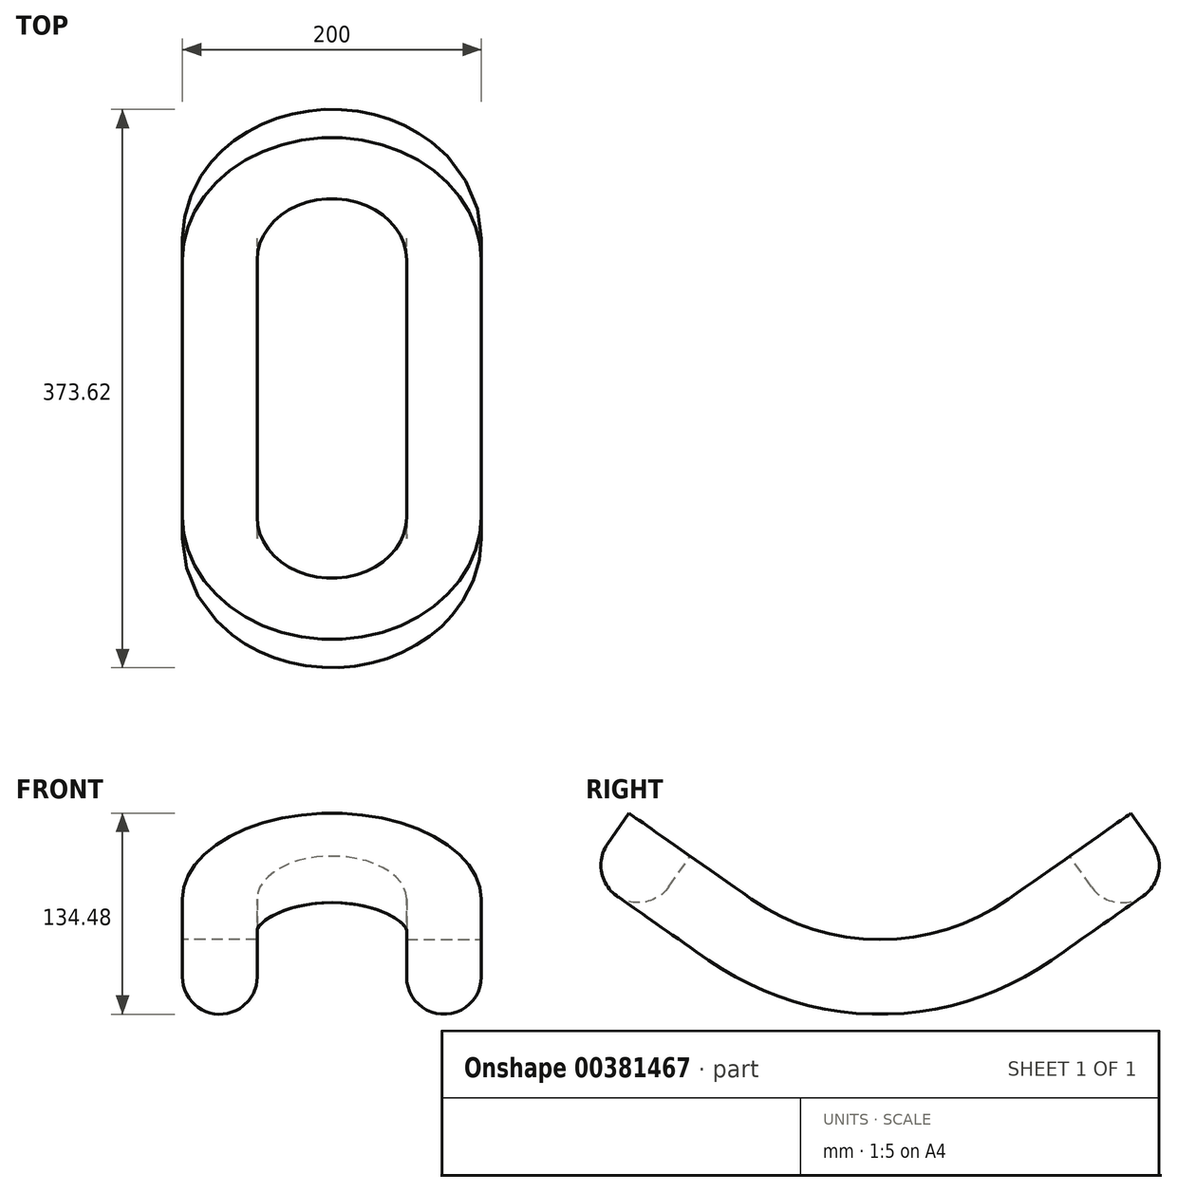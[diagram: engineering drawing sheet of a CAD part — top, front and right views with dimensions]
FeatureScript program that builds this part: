
annotation { "Feature Type Name" : "Feature", "Feature Type Description" : "" }
export const myFeature = defineFeature(function(context is Context, id is Id, definition is map)
    precondition{}
    {
        {
            var Q0;
            Q0=qCreatedBy(makeId("Right.planeOp"),FACE);
            var sketch = newSketch(context, id + "F0", { "sketchPlane" : qUnion([Q0])});
            skArc(sketch, "E0", {"start": v(0, 0) * mm, "mid": v(45.1, 6.94) * mm, "end": v(86.04, 27.13) * mm});
            skLineSegment(sketch, "E1", {"start": v(86.04, 27.13) * mm, "end": v(167.95, 84.48) * mm});
            skLineSegment(sketch, "E2", {"start": v(0, 0) * mm, "end": v(0, 150) * mm, "construction": true});
            skLineSegment(sketch, "E3", {"start": v(0, 150) * mm, "end": v(86.04, 27.13) * mm, "construction": true});
            skSolve(sketch);
        }
        {
            var Q0;
            Q0 = qConstructionFilter(qBodyType(qCreatedBy(id + "F0" ,EDGE), BodyType.WIRE), ConstructionObject.NO);
            extrude(context, id + "F1", {"bodyType" : ToolBodyType.SURFACE, "surfaceEntities" : qUnion([Q0]), "depth" : 100 * mm});
        }
        {
            var Q0;
            Q0=qCreatedBy(makeId("Front.planeOp"),FACE);
            var sketch = newSketch(context, id + "F2", { "sketchPlane" : qUnion([Q0])});
            skLineSegment(sketch, "E4.bottom", {"start": v(50, 0) * mm, "end": v(100, 0) * mm});
            skLineSegment(sketch, "E4.top", {"start": v(50, -25) * mm, "end": v(100, -25) * mm, "construction": true});
            skLineSegment(sketch, "E4.left", {"start": v(50, 0) * mm, "end": v(50, -25) * mm});
            skLineSegment(sketch, "E4.right", {"start": v(100, 0) * mm, "end": v(100, -25) * mm});
            skArc(sketch, "E5", {"start": v(50, -25) * mm, "mid": v(75, -50) * mm, "end": v(100, -25) * mm});
            skSolve(sketch);
        }
        {
            var Q0;
            Q0=makeQuery(id+"F1.opExtrude","SWEPT_FACE",FACE,{"disambiguationData":[OSD([sQuery(id+"F0.wireOp",EDGE,"E1")])]});
            var sketch = newSketch(context, id + "F3", { "sketchPlane" : qUnion([Q0])});
            skArc(sketch, "E6", {"start": v(100, -86.04) * mm, "mid": v(70.71, -156.75) * mm, "end": v(0, -186.04) * mm});
            skSolve(sketch);
        }
        {
            var Q0;
            Q0=makeQuery(id+"F2.imprint","IMPRINT",FACE,{"disambiguationData":[TD([[makeQuery(id+"F2.imprint","IMPRINT",EDGE,{"derivedFrom":sQuery(id+"F2.wireOp",EDGE,"E4.bottom")}),-1.0]])]});
            var Q1;
            Q1=makeQuery(id+"F1.opExtrude","CAP_EDGE",EDGE,{"disambiguationData":[OSD([sQuery(id+"F0.wireOp",EDGE,"E0")])],"isStart":false});
            var Q2;
            Q2=sQuery(id+"F3.wireOp",EDGE,"E6");
            sweep(context, id + "F4", {"profiles" : qUnion([Q0]), "path" : qUnion([Q1, Q2])});
        }
        {
            var Q0;
            Q0=makeQuery(id+"F4.opSweep","SWEPT_BODY",BODY,{"disambiguationData":[OSD([sQuery(id+"F2.wireOp",EDGE,"E4.bottom"),sQuery(id+"F2.wireOp",EDGE,"E4.left"),sQuery(id+"F2.wireOp",EDGE,"E4.right"),sQuery(id+"F2.wireOp",EDGE,"E5"),sQuery(id+"F3.wireOp",EDGE,"E6")])]});
            var Q1;
            Q1=qCreatedBy(makeId("Front.planeOp"),FACE);
            mirror(context, id + "F5", {"operationType" : NewBodyOperationType.ADD, "entities" : qUnion([Q0]), "mirrorPlane" : qUnion([Q1])});
        }
        {
            var Q0;
            Q0=makeQuery(id+"F4.opSweep","SWEPT_BODY",BODY,{"disambiguationData":[OSD([sQuery(id+"F2.wireOp",EDGE,"E4.bottom"),sQuery(id+"F2.wireOp",EDGE,"E4.left"),sQuery(id+"F2.wireOp",EDGE,"E4.right"),sQuery(id+"F2.wireOp",EDGE,"E5"),sQuery(id+"F3.wireOp",EDGE,"E6")])]});
            var Q1;
            Q1=qCreatedBy(makeId("Right.planeOp"),FACE);
            mirror(context, id + "F6", {"operationType" : NewBodyOperationType.ADD, "entities" : qUnion([Q0]), "mirrorPlane" : qUnion([Q1])});
        }
    });
